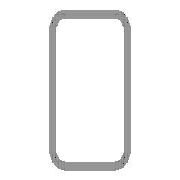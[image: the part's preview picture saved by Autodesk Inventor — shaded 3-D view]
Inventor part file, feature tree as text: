
AUTODESK INVENTOR PART (.ipt)
format: ipt  version: 2025.1 (Build 291241020, 241B)  size: 142,848 bytes
history: native  units: mm (DEFAULTED — no unit token found)
features: other x4, plane x2, split x1, sketch x1
ambient origin geometry x8: Origin, YZ Plane, XZ Plane, XY Plane, X Axis, Y Axis, Z Axis, Center Point
bodies: Solid1 (feature_tree), Body (feature_tree)
feature tree (8):
  parser-record x1  (decoder bookkeeping rows leaked as tree rows — omitted from the tree; the rows remain in map.json)
  other  "Driven Length"
  other  "Start Plane"
  other  "End Plane"
  plane  "Work Plane4"
  split  "Split1"
  sketch  "Sketch3"  dims[d3=529.948996mm d4=0.0mm d7=6.0mm d9=40.0mm d11=80.0mm d12=3.0mm d13=80.0mm d14=609.948996mm d15=20.0mm d16=40.0mm d17=90.0deg d18=529.948996mm]
  plane  "Work Plane3"
